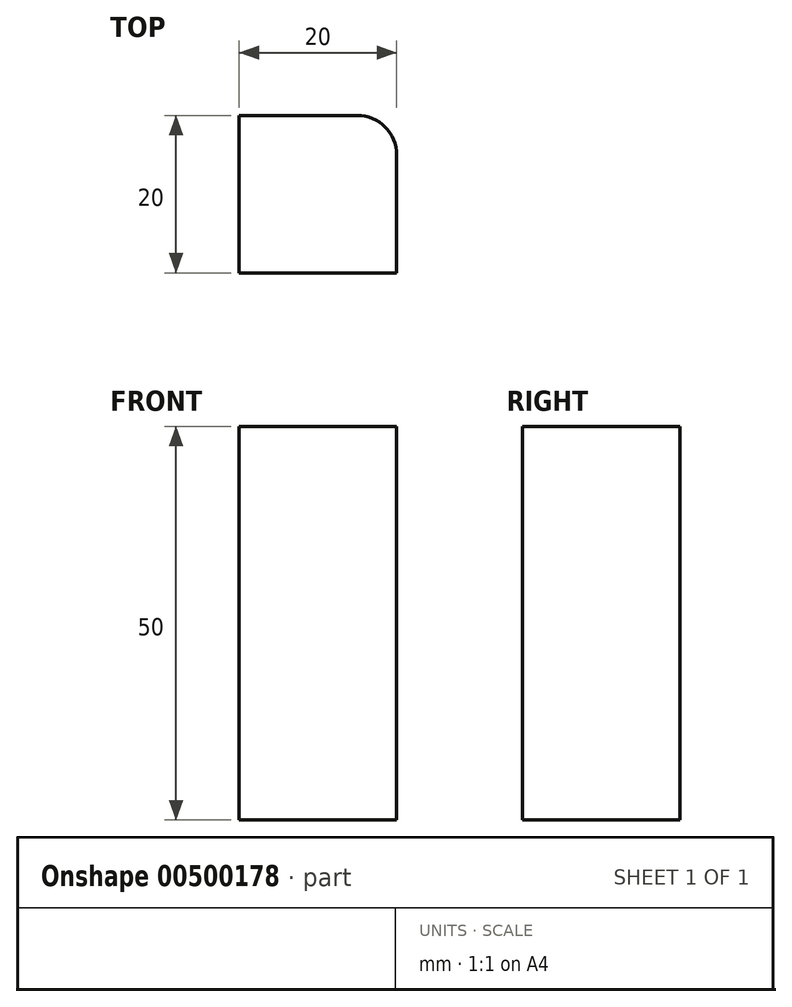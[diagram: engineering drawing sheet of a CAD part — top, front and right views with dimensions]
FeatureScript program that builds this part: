
annotation { "Feature Type Name" : "Feature", "Feature Type Description" : "" }
export const myFeature = defineFeature(function(context is Context, id is Id, definition is map)
    precondition{}
    {
        {
            var Q0;
            Q0=qCreatedBy(makeId("Top.planeOp"),FACE);
            var sketch = newSketch(context, id + "F0", { "sketchPlane" : qUnion([Q0])});
            skLineSegment(sketch, "E0.bottom", {"start": v(-11.05, 7.37) * mm, "end": v(3.95, 7.37) * mm});
            skLineSegment(sketch, "E0.top", {"start": v(-11.05, -12.63) * mm, "end": v(8.95, -12.63) * mm});
            skLineSegment(sketch, "E0.left", {"start": v(-11.05, 7.37) * mm, "end": v(-11.05, -12.63) * mm});
            skLineSegment(sketch, "E0.right", {"start": v(8.95, 2.37) * mm, "end": v(8.95, -12.63) * mm});
            skPoint(sketch, "E1.visualSharp", {"position": v(8.95, 7.37) * mm});
            skArc(sketch, "E1.filletArc", {"start": v(8.95, 2.37) * mm, "mid": v(7.49, 5.9) * mm, "end": v(3.95, 7.37) * mm});
            skSolve(sketch);
        }
        {
            var Q0;
            Q0 = qSketchRegion(id + "F0", true);
            extrude(context, id + "F1", {"entities" : qUnion([Q0]), "depth" : 25 * mm});
        }
        {
            var Q0;
            Q0=makeQuery(id+"F1.opExtrude","CAP_FACE",FACE,{"disambiguationData":[OSD([sQuery(id+"F0.wireOp",EDGE,"E0.bottom"),sQuery(id+"F0.wireOp",EDGE,"E0.top"),sQuery(id+"F0.wireOp",EDGE,"E0.left"),sQuery(id+"F0.wireOp",EDGE,"E0.right"),sQuery(id+"F0.wireOp",EDGE,"E1.filletArc")])],"isStart":false});
            extrude(context, id + "F2", {"entities" : qUnion([Q0]), "operationType" : NewBodyOperationType.ADD, "depth" : 25 * mm});
        }
    });
